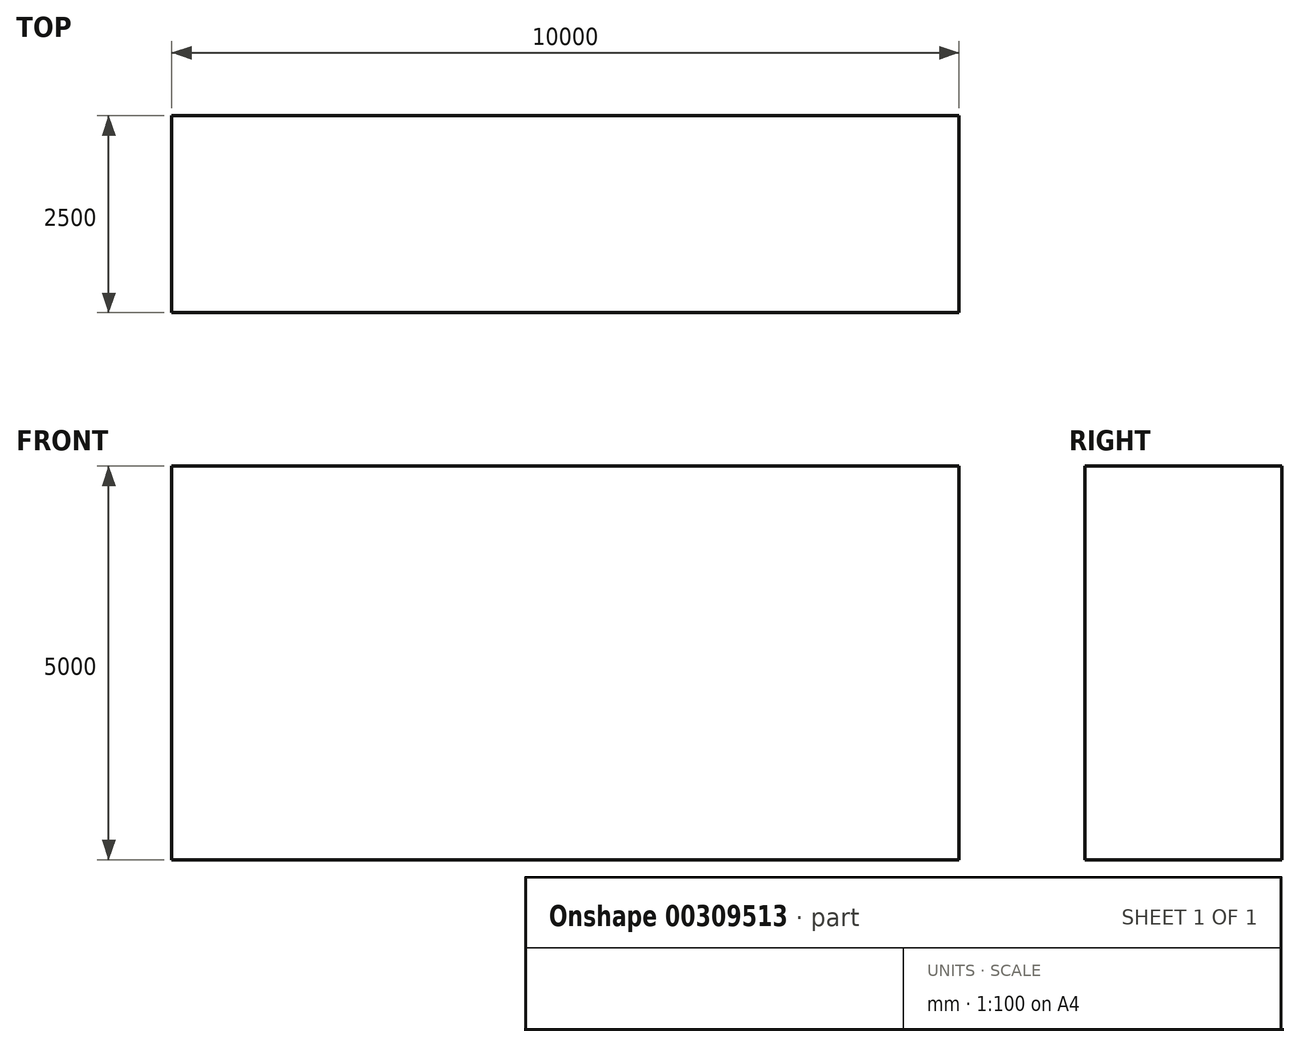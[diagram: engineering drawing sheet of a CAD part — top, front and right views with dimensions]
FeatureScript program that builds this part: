
annotation { "Feature Type Name" : "Feature", "Feature Type Description" : "" }
export const myFeature = defineFeature(function(context is Context, id is Id, definition is map)
    precondition{}
    {
        {
            var Q0;
            Q0=qCreatedBy(makeId("Front.planeOp"),FACE);
            var sketch = newSketch(context, id + "F0", { "sketchPlane" : qUnion([Q0])});
            skLineSegment(sketch, "E0.bottom", {"start": v(0, 0) * mm, "end": v(10000, 0) * mm});
            skLineSegment(sketch, "E0.top", {"start": v(0, -5000) * mm, "end": v(10000, -5000) * mm});
            skLineSegment(sketch, "E0.left", {"start": v(0, 0) * mm, "end": v(0, -5000) * mm});
            skLineSegment(sketch, "E0.right", {"start": v(10000, 0) * mm, "end": v(10000, -5000) * mm});
            skSolve(sketch);
        }
        {
            var Q0;
            Q0=makeQuery(id+"F0.imprint","IMPRINT",FACE,{"disambiguationData":[TD([[makeQuery(id+"F0.imprint","IMPRINT",EDGE,{"derivedFrom":sQuery(id+"F0.wireOp",EDGE,"E0.bottom")}),-1.0]])]});
            extrude(context, id + "F1", {"entities" : qUnion([Q0]), "depth" : 2500 * mm});
        }
    });
